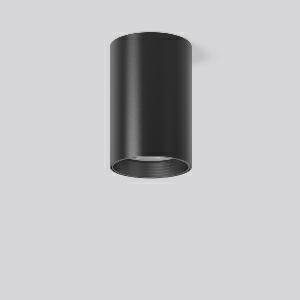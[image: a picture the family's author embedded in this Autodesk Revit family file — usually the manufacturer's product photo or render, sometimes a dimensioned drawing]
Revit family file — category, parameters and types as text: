
# Revit family: heledon_maxi_a_931229_003_2_76_3ea3
name_source: partatom
category: Lighting Fixtures
units: mm (PartAtom-declared; Revit-internal decimal feet)

## family parameters
Cut with Voids When Loaded = No
Host = Face
Light Source = No
Part Type = Normal
Room Calculation Point = No
Round Connector Dimension = Use Diameter
Shared = No

## types (1)
- HELEDON maxi A (1 x LED Modul 927, 3450 lm, 2700)
    Apparent Load = 35 VA
    Approval mark = CE
    CIE Flux Codes = 96 100 100 100 100
    Color Rendering = 92
    Color Temperature = 2700
    Default Elevation = 1800 mm
    Description = Series: HELEDON maxi
Cylindrical surface-mounted downlight. Housing: die-cast aluminium, powder-coated. Internal ceiling frame polycarbonate with bayonet mounting. Black plastic ring and recessed LED to prevent glare from the side. Optical assembly with lens made of plastic (polycarbonate) for the best homogeneous light distribution - can be changed without tools. Best colour rendering index Ra>90. Suitable for Ceiling mounting. Easy installation with a separate ceiling frame with bayonet mounting and plug connection. Driver integrated. Connected via plug-in connector. High quality converter without flickering and stroboscopic effect. The following accessories can be mounted without use of tools: interchangeable lenses, decorative glasses, honeycomb louvre, clear and frosted diffusers, white interchangeable plastic ring. 
Colour: deep black, matt (RAL 9005)
Diameter: 123 mm
Height: 183 mm
Lamp: LED
Socket: without socket
Colour temperature: 2700K
Colour rendering index (CRI): 92
System power: 35 W
Rated luminous flux: 3450 lm
Luminous efficiency: 99 lm/W
Control gear: Converter, dimmable, DALI
Protection class: I
Type of protection: IP 20
    Height = 183 mm
    Lamp = 1 x LED Modul 927
    Lamp Light Flux = 3450 lm
    Lamp count = 1
    Length = 123 mm
    Lifetime = 50000 h
    Luminous efficacy = 99 lm/W
    Manufacturer = RZB
    ModVariant = No
    Model = 931229.003.2.76
    Mounting Place = Ceiling
    Mounting Type = Surface mounted
    Number of Poles = 1
    OnlyDefault = Yes
    Power Factor = 1
    Product Name = HELEDON maxi A
    Product group = Surface mounted downlights
    ProductGroupID = 302
    Protection Class = Protection class I
    Protection Degree = IP 20
    RLX_Detail_Level = 1
    RLX_Emergency_Light_Flux = 0 lm
    RLX_Emergency_Type = 0
    RLX_Emergency_Type_DB = No
    RlxData = <blob elided: 96813 chars, md5=69dc2e41>
    Socket = socket
    Standby Power = 0 W
    System Light Flux = 3450 lm
    System Power = 35 W
    Type Comments = Product without accessories
    Type Image = 931193.003.jpg
    URL = http://relux.com
    VarID = ---
    Voltage = 230 V
    Voltage Range = 220-240 V
    Weight = 0.00 kg
    Width = 0 mm  [stored 0 ft]

note: [stored X ft] marks values corroborated as IEEE doubles in the binary element streams (Revit-internal decimal feet)

## geometry (parser evidence)
native form markers: Blend x4, Sweep x11
no freeform markers — native parametric forms only
